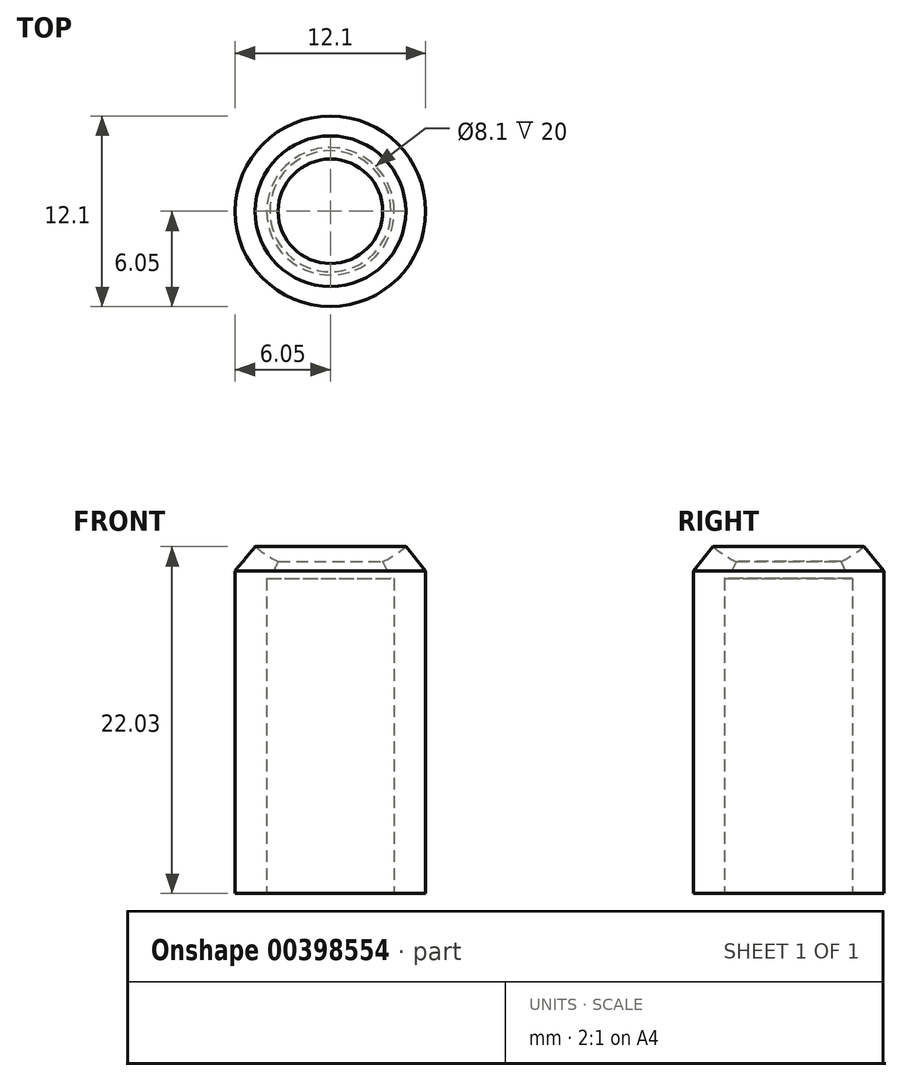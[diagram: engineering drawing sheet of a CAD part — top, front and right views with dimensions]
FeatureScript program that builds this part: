
annotation { "Feature Type Name" : "Feature", "Feature Type Description" : "" }
export const myFeature = defineFeature(function(context is Context, id is Id, definition is map)
    precondition{}
    {
        {
            var Q0;
            Q0=qCreatedBy(makeId("Front.planeOp"),FACE);
            var sketch = newSketch(context, id + "F0", { "sketchPlane" : qUnion([Q0])});
            skLineSegment(sketch, "E0.bottom", {"start": v(4.05, -10) * mm, "end": v(-4.05, -10) * mm});
            skLineSegment(sketch, "E0.top", {"start": v(0, 10) * mm, "end": v(-4.05, 10) * mm});
            skLineSegment(sketch, "E0.left", {"start": v(4.05, -10) * mm, "end": v(4.05, 10) * mm});
            skLineSegment(sketch, "E0.right", {"start": v(-4.05, -10) * mm, "end": v(-4.05, 10) * mm});
            skPoint(sketch, "E0.middle", {"position": v(0, 0) * mm});
            skCircle(sketch, "E1", {"center": v(0, 17.8) * mm, "radius": 7.5 * mm});
            skLineSegment(sketch, "E2", {"start": v(-6.05, 10) * mm, "end": v(-6.05, -10) * mm});
            skLineSegment(sketch, "E3", {"start": v(6.05, 10) * mm, "end": v(6.05, -10) * mm});
            skLineSegment(sketch, "E4", {"start": v(-6.05, 10) * mm, "end": v(-6.05, 10.5) * mm});
            skLineSegment(sketch, "E5", {"start": v(6.05, 10) * mm, "end": v(6.05, 10.5) * mm});
            skLineSegment(sketch, "E6", {"start": v(6.05, 10.5) * mm, "end": v(4.79, 12.03) * mm});
            skLineSegment(sketch, "E7", {"start": v(-6.05, 10.5) * mm, "end": v(-4.79, 12.03) * mm});
            skLineSegment(sketch, "E8", {"start": v(-6.05, -10) * mm, "end": v(-4.05, -10) * mm});
            skLineSegment(sketch, "E9", {"start": v(-4.05, -10) * mm, "end": v(-4.05, -10) * mm});
            skLineSegment(sketch, "E10", {"start": v(4.05, -10) * mm, "end": v(4.05, -10) * mm});
            skLineSegment(sketch, "E11.trimOffspring", {"start": v(4.05, -10) * mm, "end": v(6.05, -10) * mm});
            skLineSegment(sketch, "E12", {"start": v(0, -21.51) * mm, "end": v(0, 17.8) * mm});
            skLineSegment(sketch, "E13", {"start": v(-4.05, 10) * mm, "end": v(-3.85, 10) * mm});
            skLineSegment(sketch, "E14", {"start": v(-3.85, 10) * mm, "end": v(-3.32, 11.07) * mm});
            skLineSegment(sketch, "E15", {"start": v(6.25, 10) * mm, "end": v(4.05, 10) * mm});
            skLineSegment(sketch, "E16", {"start": v(4.05, 10) * mm, "end": v(3.85, 10) * mm});
            skLineSegment(sketch, "E17", {"start": v(3.85, 10) * mm, "end": v(3.32, 11.07) * mm});
            skSolve(sketch);
        }
        {
            var Q0;
            Q0=makeQuery(id+"F0.imprint","IMPRINT",FACE,{"disambiguationData":[TD([[makeQuery(id+"F0.imprint","IMPRINT",EDGE,{"derivedFrom":sQuery(id+"F0.wireOp",EDGE,"E0.right")}),1.0]])]});
            var Q1;
            Q1=sQuery(id+"F0.wireOp",EDGE,"E12");
            revolve(context, id + "F1", {"entities" : qUnion([Q0]), "axis" : qUnion([Q1]), "revolveType" : RevolveType.FULL});
        }
    });
